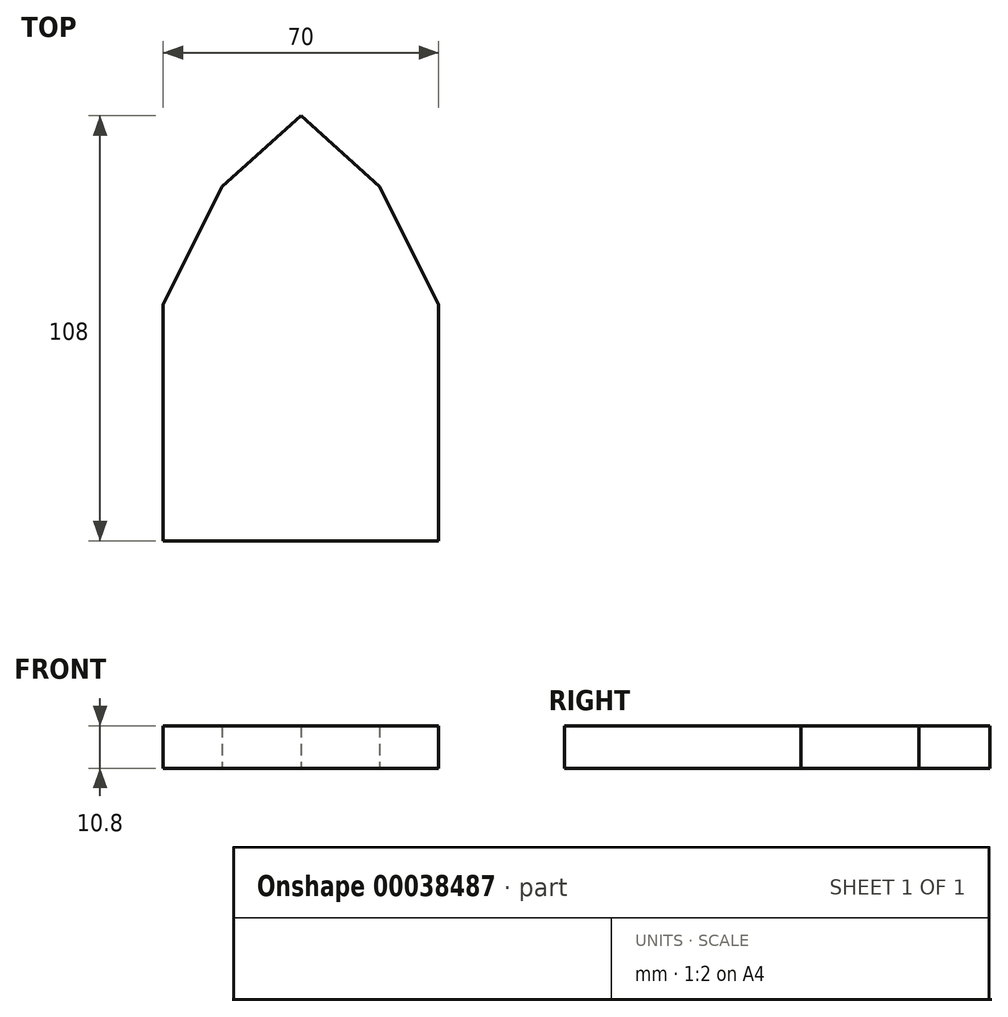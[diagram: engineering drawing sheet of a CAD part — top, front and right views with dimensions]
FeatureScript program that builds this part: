
annotation { "Feature Type Name" : "Feature", "Feature Type Description" : "" }
export const myFeature = defineFeature(function(context is Context, id is Id, definition is map)
    precondition{}
    {
        {
            var Q0;
            Q0=qCreatedBy(makeId("Top.planeOp"),FACE);
            var sketch = newSketch(context, id + "F0", { "sketchPlane" : qUnion([Q0])});
            skLineSegment(sketch, "E0.bottom", {"start": v(-35, -20.67) * mm, "end": v(35, -20.67) * mm});
            skLineSegment(sketch, "E0.top", {"start": v(-35, -50.67) * mm, "end": v(35, -50.67) * mm});
            skLineSegment(sketch, "E0.left", {"start": v(-35, -20.67) * mm, "end": v(-35, -50.67) * mm});
            skLineSegment(sketch, "E0.right", {"start": v(35, -20.67) * mm, "end": v(35, -50.67) * mm});
            skLineSegment(sketch, "E1.top", {"start": v(-35, 9.33) * mm, "end": v(35, 9.33) * mm});
            skLineSegment(sketch, "E1.left", {"start": v(-35, -20.67) * mm, "end": v(-35, 9.33) * mm});
            skLineSegment(sketch, "E1.right", {"start": v(35, -20.67) * mm, "end": v(35, 9.33) * mm});
            skLineSegment(sketch, "E2.top", {"start": v(-20, 39.33) * mm, "end": v(20, 39.33) * mm});
            skLineSegment(sketch, "E3", {"start": v(-35, 9.33) * mm, "end": v(-20, 39.33) * mm});
            skLineSegment(sketch, "E4", {"start": v(35, 9.33) * mm, "end": v(20, 39.33) * mm});
            skLineSegment(sketch, "E5", {"start": v(-20, 39.33) * mm, "end": v(0, 57.33) * mm});
            skLineSegment(sketch, "E6", {"start": v(0, 57.33) * mm, "end": v(20, 39.33) * mm});
            skLineSegment(sketch, "E7", {"start": v(0, 39.33) * mm, "end": v(0, 9.33) * mm, "construction": true});
            skLineSegment(sketch, "E8", {"start": v(0, 57.33) * mm, "end": v(0, 39.33) * mm, "construction": true});
            skSolve(sketch);
        }
        {
            var Q0;
            Q0=makeQuery(id+"F0.imprint","IMPRINT",FACE,{"disambiguationData":[TD([[makeQuery(id+"F0.imprint","IMPRINT",EDGE,{"derivedFrom":sQuery(id+"F0.wireOp",EDGE,"E0.top")}),1.0]])]});
            var Q1;
            Q1=makeQuery(id+"F0.imprint","IMPRINT",FACE,{"disambiguationData":[TD([[makeQuery(id+"F0.imprint","IMPRINT",EDGE,{"derivedFrom":sQuery(id+"F0.wireOp",EDGE,"E1.top")}),1.0]])]});
            var Q2;
            Q2=makeQuery(id+"F0.imprint","IMPRINT",FACE,{"disambiguationData":[TD([[makeQuery(id+"F0.imprint","IMPRINT",EDGE,{"derivedFrom":sQuery(id+"F0.wireOp",EDGE,"E0.bottom")}),1.0]])]});
            var Q3;
            Q3=makeQuery(id+"F0.imprint","IMPRINT",FACE,{"disambiguationData":[TD([[makeQuery(id+"F0.imprint","IMPRINT",EDGE,{"derivedFrom":sQuery(id+"F0.wireOp",EDGE,"E2.top")}),1.0]])]});
            extrude(context, id + "F1", {"entities" : qUnion([Q0, Q1, Q2, Q3]), "depth" : 10.8 * mm});
        }
    });
